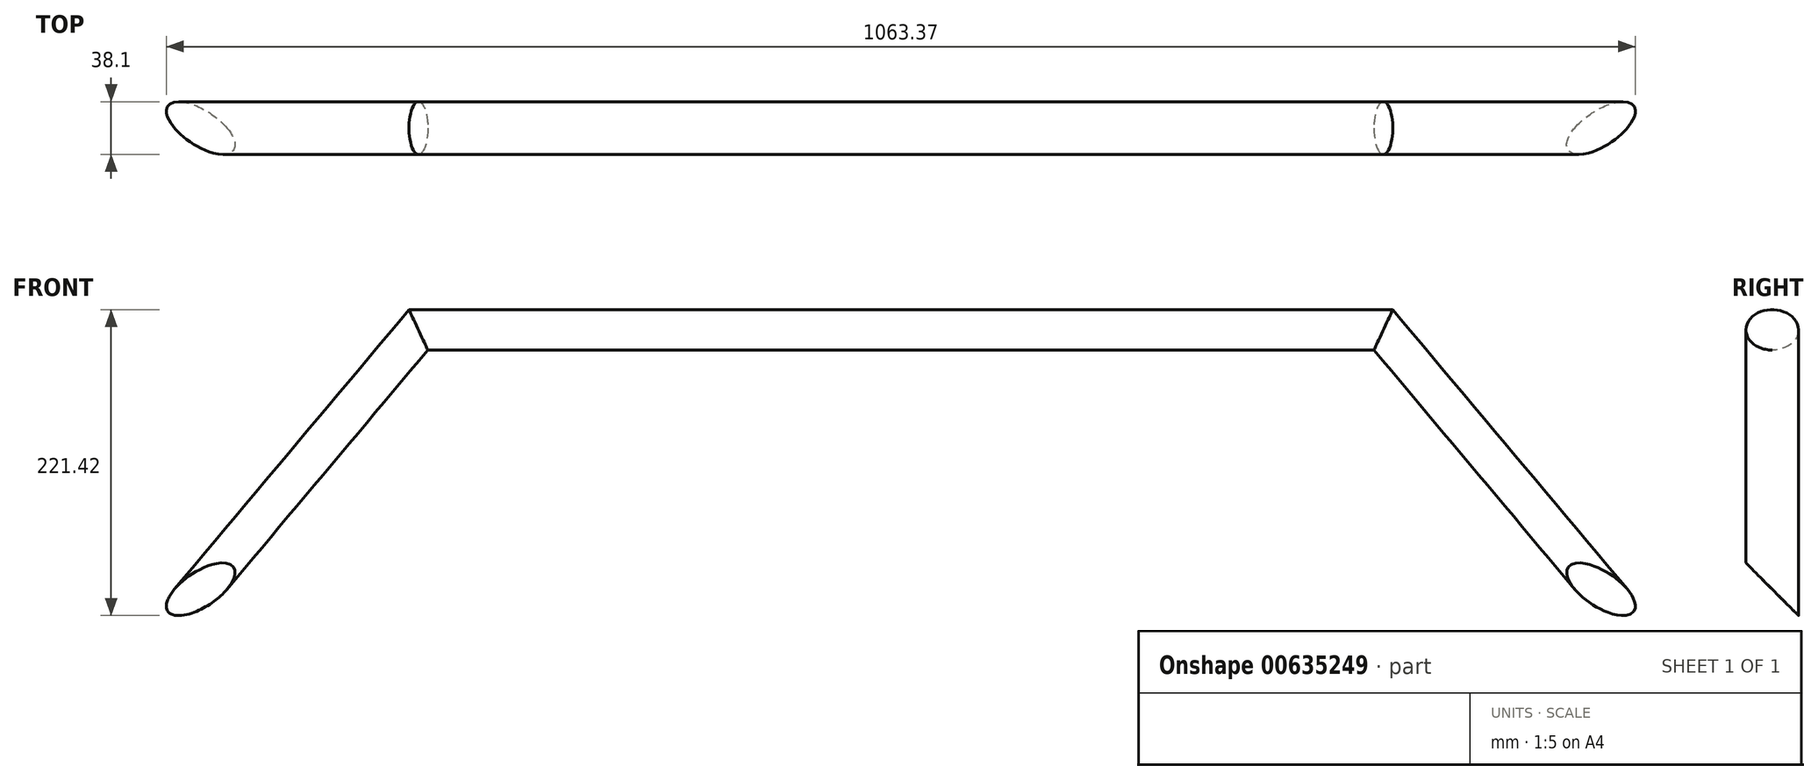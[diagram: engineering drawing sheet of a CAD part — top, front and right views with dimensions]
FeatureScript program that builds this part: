
annotation { "Feature Type Name" : "Feature", "Feature Type Description" : "" }
export const myFeature = defineFeature(function(context is Context, id is Id, definition is map)
    precondition{}
    {
        {
            var Q0;
            Q0=qCreatedBy(makeId("Top.planeOp"),FACE);
            var sketch = newSketch(context, id + "F0", { "sketchPlane" : qUnion([Q0])});
            skCircle(sketch, "E0", {"center": v(0, 0) * mm, "radius": 19.05 * mm});
            skSolve(sketch);
        }
        {
            var Q0;
            Q0=qCreatedBy(makeId("Front.planeOp"),FACE);
            var sketch = newSketch(context, id + "F1", { "sketchPlane" : qUnion([Q0])});
            skPoint(sketch, "E1.end.orphan", {"position": v(605.08, 0) * mm});
            skLineSegment(sketch, "E2", {"start": v(0, 0) * mm, "end": v(173.55, 206.83) * mm});
            skLineSegment(sketch, "E3", {"start": v(173.55, 206.83) * mm, "end": v(872.05, 206.83) * mm});
            skLineSegment(sketch, "E4", {"start": v(872.05, 206.83) * mm, "end": v(1160.53, -136.96) * mm});
            skSolve(sketch);
        }
        {
            var Q0;
            Q0=makeQuery(id+"F0.imprint","IMPRINT",FACE,{"disambiguationData":[TD([[makeQuery(id+"F0.imprint","IMPRINT",EDGE,{"derivedFrom":sQuery(id+"F0.wireOp",EDGE,"E0")}),1.0]])]});
            var Q1;
            Q1=sQuery(id+"F1.wireOp",EDGE,"E2");
            var Q2;
            Q2=sQuery(id+"F1.wireOp",EDGE,"E3");
            var Q3;
            Q3=sQuery(id+"F1.wireOp",EDGE,"E4");
            sweep(context, id + "F2", {"profiles" : qUnion([Q0]), "path" : qUnion([Q1, Q2, Q3])});
        }
        {
            var Q0;
            Q0=qCreatedBy(makeId("Front.planeOp"),FACE);
            var sketch = newSketch(context, id + "F3", { "sketchPlane" : qUnion([Q0])});
            skLineSegment(sketch, "E5.bottom", {"start": v(0, 0) * mm, "end": v(1270, 0) * mm});
            skLineSegment(sketch, "E5.top", {"start": v(0, -258.52) * mm, "end": v(1270, -258.52) * mm});
            skLineSegment(sketch, "E5.left", {"start": v(0, 0) * mm, "end": v(0, -258.52) * mm});
            skLineSegment(sketch, "E5.right", {"start": v(1270, 0) * mm, "end": v(1270, -258.52) * mm});
            skSolve(sketch);
        }
        {
            var Q0;
            Q0=makeQuery(id+"F3.imprint","IMPRINT",FACE,{"disambiguationData":[TD([[makeQuery(id+"F3.imprint","IMPRINT",EDGE,{"derivedFrom":sQuery(id+"F3.wireOp",EDGE,"E5.bottom")}),-1.0]])]});
            extrude(context, id + "F4", {"entities" : qUnion([Q0]), "operationType" : NewBodyOperationType.REMOVE, "oppositeDirection" : true, "depth" : 25.4 * mm, "offsetDistance" : 25.4 * mm, "hasSecondDirection" : true, "secondDirectionOppositeDirection" : false, "secondDirectionDepth" : 25.4 * mm});
        }
        {
            var Q0;
            Q0=qCreatedBy(makeId("Right.planeOp"),FACE);
            var sketch = newSketch(context, id + "F5", { "sketchPlane" : qUnion([Q0])});
            skLineSegment(sketch, "E6.bottom", {"start": v(-19.05, 0) * mm, "end": v(19.05, 0) * mm});
            skLineSegment(sketch, "E6.left", {"start": v(-19.05, 0) * mm, "end": v(-19.05, 38.1) * mm});
            skPoint(sketch, "E6.middle", {"position": v(0, 19.05) * mm});
            skLineSegment(sketch, "E7", {"start": v(19.05, 0) * mm, "end": v(-19.05, 38.1) * mm});
            skPoint(sketch, "E6.right.end.orphan", {"position": v(19.05, 38.1) * mm});
            skSolve(sketch);
        }
        {
            var Q0;
            Q0 = qSketchRegion(id + "F5", true);
            extrude(context, id + "F6", {"entities" : qUnion([Q0]), "operationType" : NewBodyOperationType.REMOVE, "endBound" : BoundingType.THROUGH_ALL, "oppositeDirection" : true, "depth" : 25.4 * mm, "offsetDistance" : 25.4 * mm, "hasSecondDirection" : true, "secondDirectionBound" : SecondDirectionBoundingType.THROUGH_ALL, "secondDirectionOppositeDirection" : false, "secondDirectionDepth" : 25.4 * mm});
        }
    });
